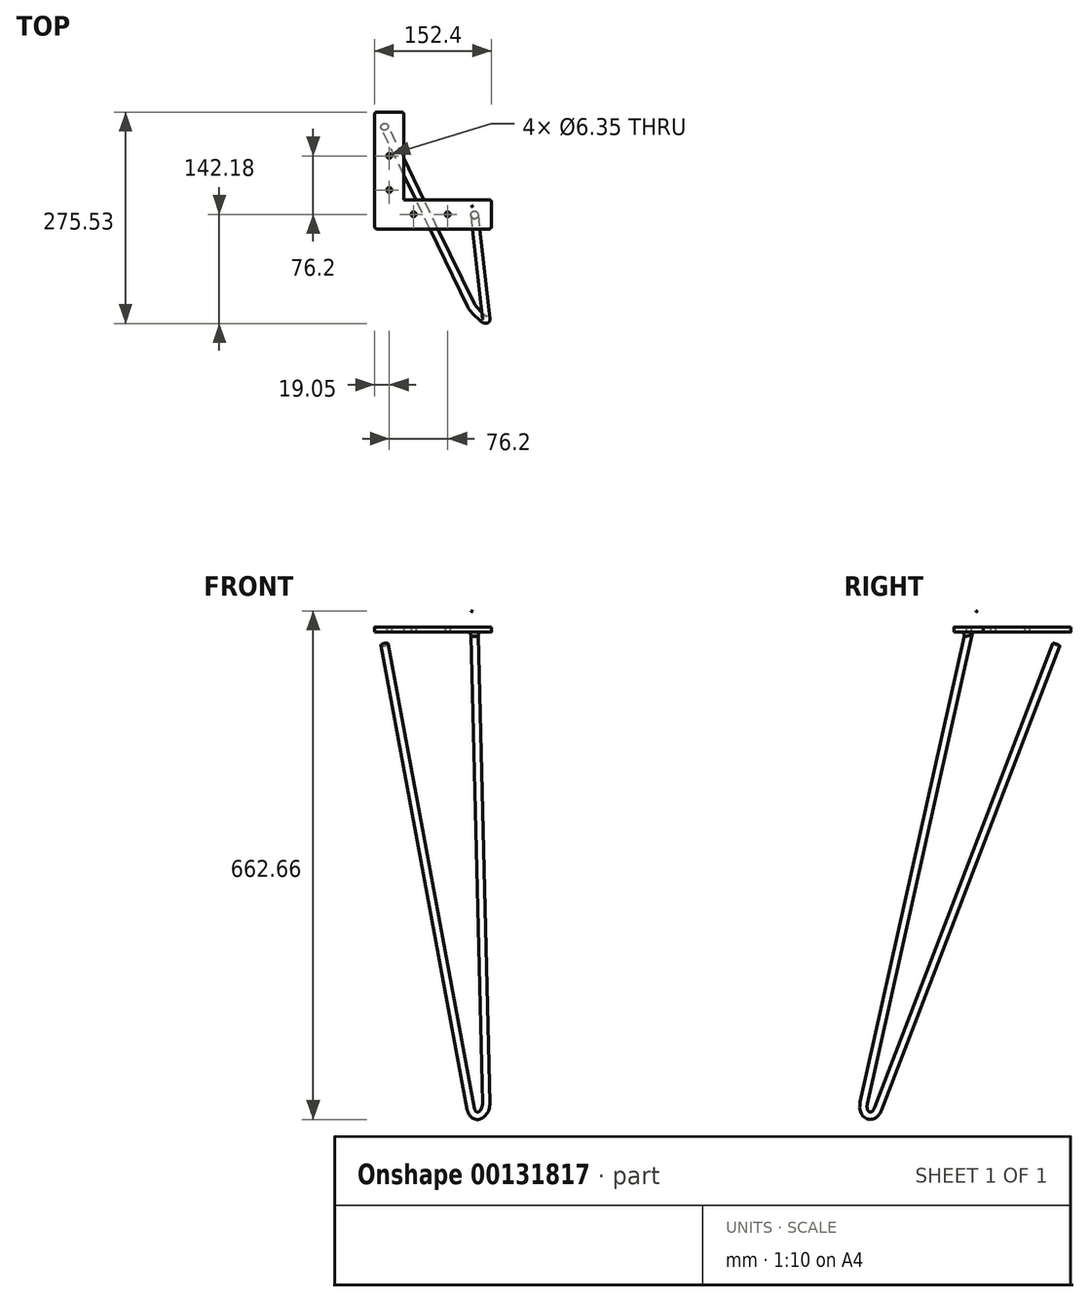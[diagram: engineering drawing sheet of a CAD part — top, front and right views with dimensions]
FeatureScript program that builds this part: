
annotation { "Feature Type Name" : "Feature", "Feature Type Description" : "" }
export const myFeature = defineFeature(function(context is Context, id is Id, definition is map)
    precondition{}
    {
        {
            var Q0;
            Q0=qCreatedBy(makeId("Top.planeOp"),FACE);
            var sketch = newSketch(context, id + "F0", { "sketchPlane" : qUnion([Q0])});
            skLineSegment(sketch, "E0", {"start": v(0, 0) * mm, "end": v(0, 152.4) * mm});
            skLineSegment(sketch, "E1", {"start": v(0, 152.4) * mm, "end": v(38.1, 152.4) * mm});
            skLineSegment(sketch, "E2", {"start": v(38.1, 152.4) * mm, "end": v(38.1, 38.1) * mm});
            skLineSegment(sketch, "E3", {"start": v(38.1, 38.1) * mm, "end": v(152.4, 38.1) * mm});
            skLineSegment(sketch, "E4", {"start": v(152.4, 38.1) * mm, "end": v(152.4, 0) * mm});
            skLineSegment(sketch, "E5", {"start": v(152.4, 0) * mm, "end": v(0, 0) * mm});
            skSolve(sketch);
        }
        {
            var Q0;
            Q0 = qSketchRegion(id + "F0", true);
            extrude(context, id + "F1", {"entities" : qUnion([Q0]), "depth" : 6.35 * mm});
        }
        {
            var Q0;
            Q0=makeQuery(id+"F1.opExtrude","CAP_FACE",FACE,{"disambiguationData":[OSD([sQuery(id+"F0.wireOp",EDGE,"E0"),sQuery(id+"F0.wireOp",EDGE,"E1"),sQuery(id+"F0.wireOp",EDGE,"E2"),sQuery(id+"F0.wireOp",EDGE,"E3"),sQuery(id+"F0.wireOp",EDGE,"E4"),sQuery(id+"F0.wireOp",EDGE,"E5")])],"isStart":true});
            cPlane(context, id + "F2", {"entities" : qUnion([Q0]), "cplaneType" : CPlaneType.OFFSET, "offset" : 762 * mm, "width" : 152.4 * mm, "height" : 152.4 * mm});
        }
        {
            var Q0;
            Q0=qCreatedBy(id+"F2.planeOp",FACE);
            var sketch = newSketch(context, id + "F3", { "sketchPlane" : qUnion([Q0])});
            skLineSegment(sketch, "E6.0.0", {"start": v(0, -152.4) * mm, "end": v(0, 0) * mm});
            skLineSegment(sketch, "E6.0.1", {"start": v(0, 0) * mm, "end": v(152.4, 0) * mm});
            skLineSegment(sketch, "E6.0.2", {"start": v(152.4, 0) * mm, "end": v(152.4, -38.1) * mm});
            skLineSegment(sketch, "E6.0.3", {"start": v(152.4, -38.1) * mm, "end": v(38.1, -38.1) * mm});
            skLineSegment(sketch, "E6.0.4", {"start": v(38.1, -38.1) * mm, "end": v(38.1, -152.4) * mm});
            skLineSegment(sketch, "E6.0.5", {"start": v(38.1, -152.4) * mm, "end": v(0, -152.4) * mm});
            skSolve(sketch);
        }
        {
            var Q0;
            Q0=makeQuery(id+"F1.opExtrude","CAP_FACE",FACE,{"disambiguationData":[OSD([sQuery(id+"F0.wireOp",EDGE,"E0"),sQuery(id+"F0.wireOp",EDGE,"E1"),sQuery(id+"F0.wireOp",EDGE,"E2"),sQuery(id+"F0.wireOp",EDGE,"E3"),sQuery(id+"F0.wireOp",EDGE,"E4"),sQuery(id+"F0.wireOp",EDGE,"E5")])],"isStart":false});
            var sketch = newSketch(context, id + "F4", { "sketchPlane" : qUnion([Q0])});
            skLineSegment(sketch, "E7", {"start": v(152.4, 19.05) * mm, "end": v(0, 19.05) * mm});
            skLineSegment(sketch, "E8", {"start": v(19.05, 152.4) * mm, "end": v(19.05, 0) * mm});
            skLineSegment(sketch, "E9", {"start": v(152.4, 38.1) * mm, "end": v(133.35, 19.05) * mm});
            skLineSegment(sketch, "E10", {"start": v(133.35, 19.05) * mm, "end": v(152.4, 0) * mm});
            skLineSegment(sketch, "E11", {"start": v(0, 152.4) * mm, "end": v(19.05, 133.35) * mm});
            skLineSegment(sketch, "E12", {"start": v(19.05, 133.35) * mm, "end": v(38.1, 152.4) * mm});
            skSolve(sketch);
        }
        {
            var Q0;
            Q0=sQuery(id+"F3.wireOp",VERTEX,"E6.0.1.start");
            var Q1;
            Q1=sQuery(id+"F4.wireOp",VERTEX,"E12.start");
            var Q2;
            Q2=sQuery(id+"F4.wireOp",VERTEX,"E10.start");
            cPlane(context, id + "F5", {"entities" : qUnion([Q0, Q1, Q2]), "cplaneType" : CPlaneType.THREE_POINT, "offset" : 25.4 * mm, "width" : 152.4 * mm, "height" : 152.4 * mm});
        }
        {
            var Q0;
            Q0=qCreatedBy(id+"F5.planeOp",FACE);
            var sketch = newSketch(context, id + "F6", { "sketchPlane" : qUnion([Q0])});
            skLineSegment(sketch, "E13.0", {"start": v(77.13, 32.17) * mm, "end": v(103.81, 35.88) * mm});
            skLineSegment(sketch, "E14.0", {"start": v(76.61, 35.88) * mm, "end": v(77.13, 32.17) * mm});
            skLineSegment(sketch, "E15.0", {"start": v(-109.66, 6.23) * mm, "end": v(-82.98, 9.93) * mm});
            skLineSegment(sketch, "E16.0", {"start": v(103.81, -747.44) * mm, "end": v(208.5, -717.79) * mm});
            skLineSegment(sketch, "E17", {"start": v(99.64, -625.6) * mm, "end": v(77.13, 32.17) * mm});
            skLineSegment(sketch, "E18", {"start": v(74.62, -629.07) * mm, "end": v(-82.98, 9.93) * mm});
            skPoint(sketch, "E19.visualSharp", {"position": v(103.81, -747.44) * mm});
            skArc(sketch, "E19.filletArc", {"start": v(74.62, -629.07) * mm, "mid": v(88.7, -638.6) * mm, "end": v(99.64, -625.6) * mm});
            skSolve(sketch);
        }
        {
            var Q0;
            Q0=sQuery(id+"F6.wireOp",EDGE,"E17");
            var Q1;
            Q1=sQuery(id+"F6.wireOp",VERTEX,"E14.0.end");
            cPlane(context, id + "F7", {"entities" : qUnion([Q0, Q1]), "cplaneType" : CPlaneType.LINE_POINT, "offset" : 25.4 * mm, "width" : 152.4 * mm, "height" : 152.4 * mm});
        }
        {
            var Q0;
            Q0=qCreatedBy(id+"F7.planeOp",FACE);
            var sketch = newSketch(context, id + "F8", { "sketchPlane" : qUnion([Q0])});
            skPoint(sketch, "E20.0", {"position": v(130.22, 18.89) * mm});
            skCircle(sketch, "E21", {"center": v(130.22, 18.89) * mm, "radius": 4.76 * mm});
            skSolve(sketch);
        }
        {
            var Q0;
            Q0=makeQuery(id+"F8.imprint","IMPRINT",FACE,{"disambiguationData":[TD([[makeQuery(id+"F8.imprint","IMPRINT",EDGE,{"derivedFrom":sQuery(id+"F8.wireOp",EDGE,"E21")}),1.0]])]});
            var Q1;
            Q1=sQuery(id+"F6.wireOp",EDGE,"E17");
            var Q2;
            Q2=sQuery(id+"F6.wireOp",EDGE,"E19.filletArc");
            var Q3;
            Q3=sQuery(id+"F6.wireOp",EDGE,"E18");
            sweep(context, id + "F9", {"operationType" : NewBodyOperationType.ADD, "profiles" : qUnion([Q0]), "path" : qUnion([Q1, Q2, Q3])});
        }
        {
            var Q0;
            Q0=makeQuery(id+"F9.boolean.opBoolean","INTERSECT",EDGE,{"derivedFrom":[makeQuery(id+"F1.opExtrude","CAP_FACE",FACE,{"disambiguationData":[OSD([sQuery(id+"F0.wireOp",EDGE,"E0"),sQuery(id+"F0.wireOp",EDGE,"E1"),sQuery(id+"F0.wireOp",EDGE,"E2"),sQuery(id+"F0.wireOp",EDGE,"E3"),sQuery(id+"F0.wireOp",EDGE,"E4"),sQuery(id+"F0.wireOp",EDGE,"E5")])],"isStart":true}),makeQuery(id+"F9.opSweep","SWEPT_FACE",FACE,{"disambiguationData":[OSD([sQuery(id+"F6.wireOp",EDGE,"E17"),sQuery(id+"F8.wireOp",EDGE,"E21")])]})]});
            var Q1;
            Q1=makeQuery(id+"F9.boolean.opBoolean","INTERSECT",EDGE,{"derivedFrom":[makeQuery(id+"F1.opExtrude","CAP_FACE",FACE,{"disambiguationData":[OSD([sQuery(id+"F0.wireOp",EDGE,"E0"),sQuery(id+"F0.wireOp",EDGE,"E1"),sQuery(id+"F0.wireOp",EDGE,"E2"),sQuery(id+"F0.wireOp",EDGE,"E3"),sQuery(id+"F0.wireOp",EDGE,"E4"),sQuery(id+"F0.wireOp",EDGE,"E5")])],"isStart":true}),makeQuery(id+"F9.opSweep","SWEPT_FACE",FACE,{"disambiguationData":[OSD([sQuery(id+"F6.wireOp",EDGE,"E18"),sQuery(id+"F8.wireOp",EDGE,"E21")])]})]});
            fillet(context, id + "F10", {"entities" : qUnion([Q0, Q1]), "radius" : 5.08 * mm, "tangentPropagation" : true, "allowEdgeOverflow" : false});
        }
        {
            var Q0;
            Q0=makeQuery(id+"F1.opExtrude","CAP_FACE",FACE,{"disambiguationData":[OSD([sQuery(id+"F0.wireOp",EDGE,"E0"),sQuery(id+"F0.wireOp",EDGE,"E1"),sQuery(id+"F0.wireOp",EDGE,"E2"),sQuery(id+"F0.wireOp",EDGE,"E3"),sQuery(id+"F0.wireOp",EDGE,"E4"),sQuery(id+"F0.wireOp",EDGE,"E5")])],"isStart":false});
            var sketch = newSketch(context, id + "F11", { "sketchPlane" : qUnion([Q0])});
            skCircle(sketch, "E22", {"center": v(19.73, 133.25) * mm, "radius": 9.93 * mm});
            skPoint(sketch, "E22.centerSnap0", {"position": v(19.73, 138.14) * mm});
            skCircle(sketch, "E23", {"center": v(133.25, 19.73) * mm, "radius": 11.5 * mm});
            skPoint(sketch, "E23.centerSnap0", {"position": v(138.14, 19.73) * mm});
            skSolve(sketch);
        }
        {
            var Q0;
            Q0 = qSketchRegion(id + "F11", true);
            extrude(context, id + "F12", {"entities" : qUnion([Q0]), "operationType" : NewBodyOperationType.REMOVE, "depth" : 25.4 * mm});
        }
        {
            var Q0;
            Q0=makeQuery(id+"F1.opExtrude","CAP_FACE",FACE,{"disambiguationData":[OSD([sQuery(id+"F0.wireOp",EDGE,"E0"),sQuery(id+"F0.wireOp",EDGE,"E1"),sQuery(id+"F0.wireOp",EDGE,"E2"),sQuery(id+"F0.wireOp",EDGE,"E3"),sQuery(id+"F0.wireOp",EDGE,"E4"),sQuery(id+"F0.wireOp",EDGE,"E5")])],"isStart":true});
            var sketch = newSketch(context, id + "F13", { "sketchPlane" : qUnion([Q0])});
            skLineSegment(sketch, "E24", {"start": v(152.4, -19.05) * mm, "end": v(0, -19.05) * mm, "construction": true});
            skPoint(sketch, "E25.endSnap0", {"position": v(20.18, -141.26) * mm});
            skLineSegment(sketch, "E26", {"start": v(19.05, -152.4) * mm, "end": v(19.05, 0) * mm, "construction": true});
            skCircle(sketch, "E27", {"center": v(95.25, -19.05) * mm, "radius": 3.18 * mm});
            skCircle(sketch, "E28", {"center": v(50.8, -19.05) * mm, "radius": 3.18 * mm});
            skCircle(sketch, "E29", {"center": v(19.05, -50.8) * mm, "radius": 3.18 * mm});
            skCircle(sketch, "E30", {"center": v(19.05, -95.25) * mm, "radius": 3.18 * mm});
            skSolve(sketch);
        }
        {
            var Q0;
            Q0 = qSketchRegion(id + "F13", true);
            extrude(context, id + "F14", {"entities" : qUnion([Q0]), "operationType" : NewBodyOperationType.REMOVE, "oppositeDirection" : true, "depth" : 25.4 * mm});
        }
        {
            var Q0;
            Q0=makeQuery(id+"F1.opExtrude","SWEPT_EDGE",EDGE,{"disambiguationData":[OSD([sQuery(id+"F0.wireOp",EDGE,"E4"),sQuery(id+"F0.wireOp",EDGE,"E5")])]});
            var Q1;
            Q1=makeQuery(id+"F1.opExtrude","SWEPT_EDGE",EDGE,{"disambiguationData":[OSD([sQuery(id+"F0.wireOp",EDGE,"E3"),sQuery(id+"F0.wireOp",EDGE,"E4")])]});
            var Q2;
            Q2=makeQuery(id+"F1.opExtrude","SWEPT_EDGE",EDGE,{"disambiguationData":[OSD([sQuery(id+"F0.wireOp",EDGE,"E0"),sQuery(id+"F0.wireOp",EDGE,"E5")])]});
            var Q3;
            Q3=makeQuery(id+"F1.opExtrude","SWEPT_EDGE",EDGE,{"disambiguationData":[OSD([sQuery(id+"F0.wireOp",EDGE,"E0"),sQuery(id+"F0.wireOp",EDGE,"E1")])]});
            var Q4;
            Q4=makeQuery(id+"F1.opExtrude","SWEPT_EDGE",EDGE,{"disambiguationData":[OSD([sQuery(id+"F0.wireOp",EDGE,"E1"),sQuery(id+"F0.wireOp",EDGE,"E2")])]});
            fillet(context, id + "F15", {"entities" : qUnion([Q0, Q1, Q2, Q3, Q4]), "radius" : 3.17 * mm, "tangentPropagation" : true, "allowEdgeOverflow" : false});
        }
    });
